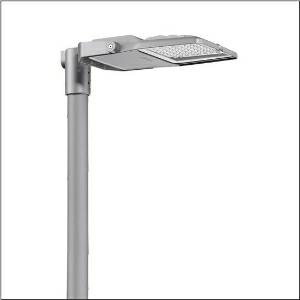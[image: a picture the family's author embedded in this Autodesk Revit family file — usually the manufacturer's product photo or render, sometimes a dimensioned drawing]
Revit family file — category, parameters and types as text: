
# Revit family: floodlight_fl_21_iq_mini___pl43_5xa7772b2a3a_a256
name_source: partatom
category: Lighting Fixtures
units: mm (PartAtom-declared; Revit-internal decimal feet)

## family parameters
Cut with Voids When Loaded = No
Host = Face
Light Source = No
Part Type = Normal
Room Calculation Point = No
Round Connector Dimension = Use Diameter
Shared = No

## types (1)
- --- (1 x LED, 6400 lm, 45.5 W, 3000K)
    Apparent Load = 46 VA
    CIE Flux Codes = 27 78 99 100 100
    Color Rendering = 70
    Color Temperature = 3000K
    Default Elevation = 1800 mm
    Description = Floodlight FL 21 iQ mini, floodlight, primary light control with lens, of PMMA, primary optical cover: protective disc, of toughened safety glass, transparent, light distribution: PL43, light emission: direct distribution, installation type: surface-mounted, LED, High Power LED, rated luminous flux: 6.400lm, luminous efficacy: 141lm/W, light colour: 730, colour temperature: 3000K, control gear: iQ Street-Remote/DALI, control: Auto-Match, Temp-Guard, Night-Set, Smart-Wire, Desk-Remote (wireless, voltage-free reading and setting of iQ features in the workshop via application-optimized NFC function/RFID function), optimised constant luminous flux control (CLO 2.0), Light-Fading, Lumen-Switch, with terminal, 6-pole, mains connection: 220..240V, AC, 50/60Hz, start of lifetime: 46W, end of service life: 48W, reduction: 22W, luminaire housing, of diecast aluminium, powder-coated, Siteco® metallic grey (DB 702S), corrosivity category C5 mid according to DIN EN ISO 12944, suitable for swimming pools, chlorine-resistant, sealing non-destructively replaceable, please order mast flange separately, mast bracket, of steel, galvanised, powder-coated, protection rating (complete): IP66, insulation class (complete): insulation class II (safety insulation), certification: CE, ENEC, VDE, protection symbol: D, impact resistance: IK08, permissible operating ambient temperature: -40..+40°C, permissible operating ambient temperature for outdoor applications: -40..+50°C, standard: DIN EN 12944, LABS conformity tested according to VDMA 24364:2018-05, packaging unit: 1 piece

Light Distribution: PL43
    Height = 70 mm
    Lamp = 1 x LED
    Lamp Light Flux = 6400 lm
    Lamp Power = 45.5 W
    Lamp count = 1
    Length = 485 mm
    Luminous efficacy = 141 lm/W
    Manufacturer = Siteco
    ModVariant = No
    Model = 5XA7772B2A3A
    Number of Poles = 1
    OnlyDefault = Yes
    Power Factor = 1
    Product Name = Floodlight FL 21 iQ mini | PL43
    Product group = floodlight | pylon annexe
    ProductGroupID = 6200
    Protection Class = Protection class II
    Protection Degree = IP 66
    RLX_Detail_Level = 1
    RLX_Emergency_Light_Flux = 0 lm
    RLX_Emergency_Type = 0
    RLX_Emergency_Type_DB = No
    RlxData = <blob elided: 101185 chars, md5=d94e5411>
    Socket = socket
    Standby Power = 0 W
    System Light Flux = 6400 lm
    System Power = 46 W
    Type Comments = factory setting: luminous flux: 100 % | dim-lin: 254 | 463 mA
    Type Image = l_1007125.jpg
    URL = http://relux.com
    VarID = @adj_162790
    Voltage = 0 V
    Weight = 0.00 kg
    Width = 337 mm

## geometry (parser evidence)
native form markers: Blend x4, Sweep x12
no freeform markers — native parametric forms only
